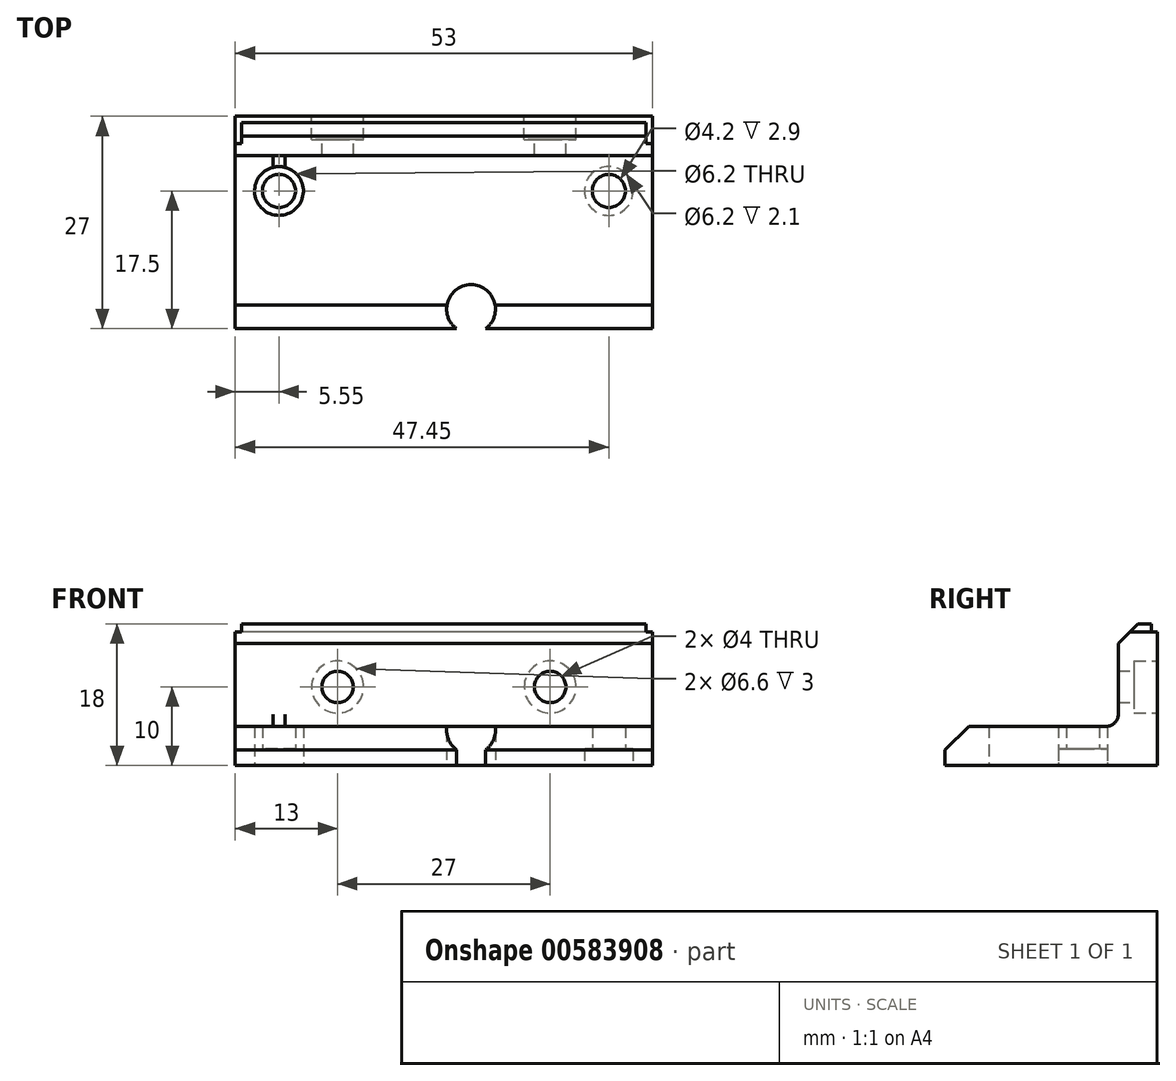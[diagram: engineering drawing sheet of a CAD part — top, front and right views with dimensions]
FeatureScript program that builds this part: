
annotation { "Feature Type Name" : "Feature", "Feature Type Description" : "" }
export const myFeature = defineFeature(function(context is Context, id is Id, definition is map)
    precondition{}
    {
        {
            var Q0;
            Q0=qCreatedBy(makeId("Top.planeOp"),FACE);
            var sketch = newSketch(context, id + "F0", { "sketchPlane" : qUnion([Q0])});
            skLineSegment(sketch, "E0.bottom", {"start": v(-26.5, 0) * mm, "end": v(26.5, 0) * mm});
            skLineSegment(sketch, "E0.top", {"start": v(-26.5, -27) * mm, "end": v(26.5, -27) * mm});
            skLineSegment(sketch, "E0.left", {"start": v(-26.5, 0) * mm, "end": v(-26.5, -27) * mm});
            skLineSegment(sketch, "E0.right", {"start": v(26.5, 0) * mm, "end": v(26.5, -27) * mm});
            skPoint(sketch, "E1", {"position": v(0, 0) * mm});
            skLineSegment(sketch, "E2", {"start": v(0, -27) * mm, "end": v(0, 0) * mm, "construction": true});
            skLineSegment(sketch, "E3", {"start": v(-20.95, -9.5) * mm, "end": v(20.95, -9.5) * mm, "construction": true});
            skPoint(sketch, "E4", {"position": v(0, -9.5) * mm});
            skCircle(sketch, "E5", {"center": v(20.95, -9.5) * mm, "radius": 2.1 * mm});
            skCircle(sketch, "E6.MirrorC", {"center": v(-20.95, -9.5) * mm, "radius": 2.1 * mm});
            skPoint(sketch, "E7", {"position": v(0, -24.5) * mm});
            skCircle(sketch, "E8", {"center": v(3.45, -24.5) * mm, "radius": 3.1 * mm});
            skCircle(sketch, "E9", {"center": v(20.95, -9.5) * mm, "radius": 3.1 * mm});
            skCircle(sketch, "E10.MirrorC", {"center": v(-20.95, -9.5) * mm, "radius": 3.1 * mm});
            skLineSegment(sketch, "E11", {"start": v(-26.5, -5) * mm, "end": v(26.5, -5) * mm});
            skSolve(sketch);
        }
        {
            var Q0;
            Q0=makeQuery(id+"F0.imprint","IMPRINT",FACE,{"disambiguationData":[TD([[makeQuery(id+"F0.imprint","IMPRINT",EDGE,{"derivedFrom":sQuery(id+"F0.wireOp",EDGE,"E0.bottom")}),-1.0]])]});
            var Q1;
            Q1=makeQuery(id+"F0.imprint","IMPRINT",FACE,{"disambiguationData":[TD([[makeQuery(id+"F0.imprint","IMPRINT",EDGE,{"derivedFrom":sQuery(id+"F0.wireOp",EDGE,"E6.MirrorC")}),1.0]])]});
            var Q2;
            Q2=makeQuery(id+"F0.imprint","IMPRINT",FACE,{"disambiguationData":[TD([[makeQuery(id+"F0.imprint","IMPRINT",EDGE,{"derivedFrom":sQuery(id+"F0.wireOp",EDGE,"E5")}),-1.0]])]});
            var Q3;
            Q3=makeQuery(id+"F0.imprint","IMPRINT",FACE,{"disambiguationData":[TD([[makeQuery(id+"F0.imprint","IMPRINT",EDGE,{"derivedFrom":sQuery(id+"F0.wireOp",EDGE,"E9")}),-1.0]])]});
            extrude(context, id + "F1", {"entities" : qUnion([Q0, Q1, Q2, Q3]), "depth" : 5 * mm, "offsetDistance" : 25 * mm});
        }
        {
            var Q0;
            Q0=makeQuery(id+"F0.imprint","IMPRINT",FACE,{"disambiguationData":[TD([[makeQuery(id+"F0.imprint","IMPRINT",EDGE,{"derivedFrom":sQuery(id+"F0.wireOp",EDGE,"E5")}),-1.0]])]});
            var Q1;
            Q1=makeQuery(id+"F0.imprint","IMPRINT",FACE,{"disambiguationData":[TD([[makeQuery(id+"F0.imprint","IMPRINT",EDGE,{"derivedFrom":sQuery(id+"F0.wireOp",EDGE,"E6.MirrorC")}),1.0]])]});
            extrude(context, id + "F2", {"entities" : qUnion([Q0, Q1]), "operationType" : NewBodyOperationType.REMOVE, "depth" : 2.1 * mm, "offsetDistance" : 25 * mm});
        }
        {
            var Q0;
            {var subQ0=sQuery(id+"F0.wireOp",EDGE,"E0.bottom");Q0=makeQuery(id+"F0.imprint","IMPRINT",FACE,{"disambiguationData":[TD([[makeQuery(id+"F0.imprint","IMPRINT",EDGE,{"derivedFrom":subQ0}),-1.0]])]});}
            extrude(context, id + "F3", {"entities" : qUnion([Q0]), "operationType" : NewBodyOperationType.ADD, "depth" : 18 * mm, "offsetDistance" : 25 * mm});
        }
        {
            var Q0;
            {var subQ0=sQuery(id+"F0.wireOp",EDGE,"E0.bottom");Q0=makeQuery(id+"F3.boolean.opBoolean","MERGE",FACE,{"derivedFrom":[makeQuery(id+"F1.opExtrude","SWEPT_FACE",FACE,{"disambiguationData":[OSD([subQ0])]}),makeQuery(id+"F3.opExtrude","SWEPT_FACE",FACE,{"disambiguationData":[OSD([subQ0])]})]});}
            var sketch = newSketch(context, id + "F4", { "sketchPlane" : qUnion([Q0])});
            skPoint(sketch, "E12.0", {"position": v(-26.5, 18) * mm});
            skPoint(sketch, "E12.1", {"position": v(26.5, 18) * mm});
            skLineSegment(sketch, "E13.bottom", {"start": v(-26.5, 18) * mm, "end": v(26.5, 18) * mm});
            skLineSegment(sketch, "E13.top", {"start": v(-26.5, 17) * mm, "end": v(26.5, 17) * mm});
            skLineSegment(sketch, "E13.left", {"start": v(-26.5, 18) * mm, "end": v(-26.5, 17) * mm});
            skLineSegment(sketch, "E13.right", {"start": v(26.5, 18) * mm, "end": v(26.5, 17) * mm});
            skLineSegment(sketch, "E14", {"start": v(-26.5, 5) * mm, "end": v(26.5, 5) * mm, "construction": true});
            skLineSegment(sketch, "E15", {"start": v(13.5, 17) * mm, "end": v(13.5, 0) * mm, "construction": true});
            skPoint(sketch, "E16", {"position": v(13.5, 10) * mm});
            skPoint(sketch, "E17.MirrorP", {"position": v(-13.5, 10) * mm});
            skLineSegment(sketch, "E18", {"start": v(-25.7, 18) * mm, "end": v(-25.7, 17) * mm});
            skLineSegment(sketch, "E19.MirrorCS", {"start": v(25.7, 18) * mm, "end": v(25.7, 17) * mm});
            skSolve(sketch);
        }
        {
            var Q0;
            Q0=makeQuery(id+"F4.imprint","IMPRINT",FACE,{"disambiguationData":[TD([[makeQuery(id+"F4.imprint","IMPRINT",EDGE,{"derivedFrom":sQuery(id+"F4.wireOp",EDGE,"E13.bottom")}),1.0]])]});
            extrude(context, id + "F5", {"entities" : qUnion([Q0]), "operationType" : NewBodyOperationType.REMOVE, "oppositeDirection" : true, "depth" : .8 * mm, "offsetDistance" : 25 * mm});
        }
        {
            var Q0;
            {var subQ0=sQuery(id+"F4.wireOp",EDGE,"E13.left");Q0=makeQuery(id+"F4.imprint","IMPRINT",FACE,{"disambiguationData":[TD([[makeQuery(id+"F4.imprint","IMPRINT",EDGE,{"derivedFrom":subQ0}),1.0]])]});}
            var Q1;
            {var subQ0=sQuery(id+"F4.wireOp",EDGE,"E13.right");Q1=makeQuery(id+"F4.imprint","IMPRINT",FACE,{"disambiguationData":[TD([[makeQuery(id+"F4.imprint","IMPRINT",EDGE,{"derivedFrom":subQ0}),-1.0]])]});}
            extrude(context, id + "F6", {"entities" : qUnion([Q0, Q1]), "operationType" : NewBodyOperationType.REMOVE, "oppositeDirection" : true, "depth" : 25 * mm, "offsetDistance" : 25 * mm});
        }
        {
            var Q0;
            Q0=sQuery(id+"F4.wireOp",VERTEX,"E16");
            var Q1;
            Q1=sQuery(id+"F4.wireOp",VERTEX,"E17.MirrorP");
            var Q2;
            Q2=makeQuery(id+"F1.opExtrude","SWEPT_BODY",BODY,{"disambiguationData":[OSD([sQuery(id+"F0.wireOp",EDGE,"E0.bottom"),sQuery(id+"F0.wireOp",EDGE,"E0.top"),sQuery(id+"F0.wireOp",EDGE,"E0.left"),sQuery(id+"F0.wireOp",EDGE,"E0.right"),sQuery(id+"F0.wireOp",EDGE,"E5"),sQuery(id+"F0.wireOp",EDGE,"E6.MirrorC"),sQuery(id+"F0.wireOp",EDGE,"E8")])]});
            hole(context, id + "F7", {"style" : HoleStyle.C_BORE, "endStyle" : HoleEndStyle.THROUGH, "standardTappedOrClearance" : lookupTablePath({ "standard" : "ISO", "size" : "4", "type" : "Drilled" }), "standardBlindInLast" : lookupTablePath({ "standard" : "ISO", "size" : "4", "type" : "Drilled" }), "holeDiameter" : 4 * mm, "cBoreDiameter" : 6.6 * mm, "cBoreDepth" : 3 * mm, "majorDiameter" : 5 * mm, "isTappedThrough" : true, "tappedDepth" : 6.2 * mm, "tapClearance" : 3, "startFromSketch" : true, "locations" : qUnion([Q0, Q1]), "scope" : qUnion([Q2])});
        }
        {
            var Q0;
            Q0=makeQuery(id+"F3.opExtrude","CAP_EDGE",EDGE,{"disambiguationData":[OSD([sQuery(id+"F0.wireOp",EDGE,"E11")])],"isStart":false});
            chamfer(context, id + "F8", {"entities" : qUnion([Q0]), "width" : 2.5 * mm, "tangentPropagation" : true});
        }
        {
            var Q0;
            Q0=makeQuery(id+"F3.boolean.opBoolean","INTERSECT",EDGE,{"derivedFrom":[makeQuery(id+"F1.opExtrude","CAP_FACE",FACE,{"disambiguationData":[OSD([sQuery(id+"F0.wireOp",EDGE,"E0.bottom"),sQuery(id+"F0.wireOp",EDGE,"E0.top"),sQuery(id+"F0.wireOp",EDGE,"E0.left"),sQuery(id+"F0.wireOp",EDGE,"E0.right"),sQuery(id+"F0.wireOp",EDGE,"E5"),sQuery(id+"F0.wireOp",EDGE,"E6.MirrorC"),sQuery(id+"F0.wireOp",EDGE,"E8")])],"isStart":false}),makeQuery(id+"F3.opExtrude","SWEPT_FACE",FACE,{"disambiguationData":[OSD([sQuery(id+"F0.wireOp",EDGE,"E11")])]})]});
            fillet(context, id + "F9", {"entities" : qUnion([Q0]), "radius" : 1.5 * mm, "tangentPropagation" : true, "allowEdgeOverflow" : false});
        }
        {
            var Q0;
            {var subQ0=sQuery(id+"F0.wireOp",EDGE,"E0.top");Q0=makeQuery(id+"F1.opExtrude","CAP_EDGE",EDGE,{"disambiguationData":[OSD([subQ0]),TDD([makeQuery(id+"F0.imprint","IMPRINT",EDGE,{"disambiguationData":[TD([[makeQuery(id+"F0.imprint","INTERSECT",VERTEX,{"derivedFrom":[subQ0,sQuery(id+"F0.wireOp",EDGE,"E0.right")]}),1.0]])],"derivedFrom":subQ0})])],"isStart":false});}
            var Q1;
            {var subQ0=sQuery(id+"F0.wireOp",EDGE,"E0.top");Q1=makeQuery(id+"F1.opExtrude","CAP_EDGE",EDGE,{"disambiguationData":[OSD([subQ0]),TDD([makeQuery(id+"F0.imprint","IMPRINT",EDGE,{"disambiguationData":[TD([[makeQuery(id+"F0.imprint","INTERSECT",VERTEX,{"derivedFrom":[subQ0,sQuery(id+"F0.wireOp",EDGE,"E0.left")]}),-1.0]])],"derivedFrom":subQ0})])],"isStart":false});}
            chamfer(context, id + "F10", {"entities" : qUnion([Q0, Q1]), "width" : 3 * mm, "tangentPropagation" : true});
        }
    });
